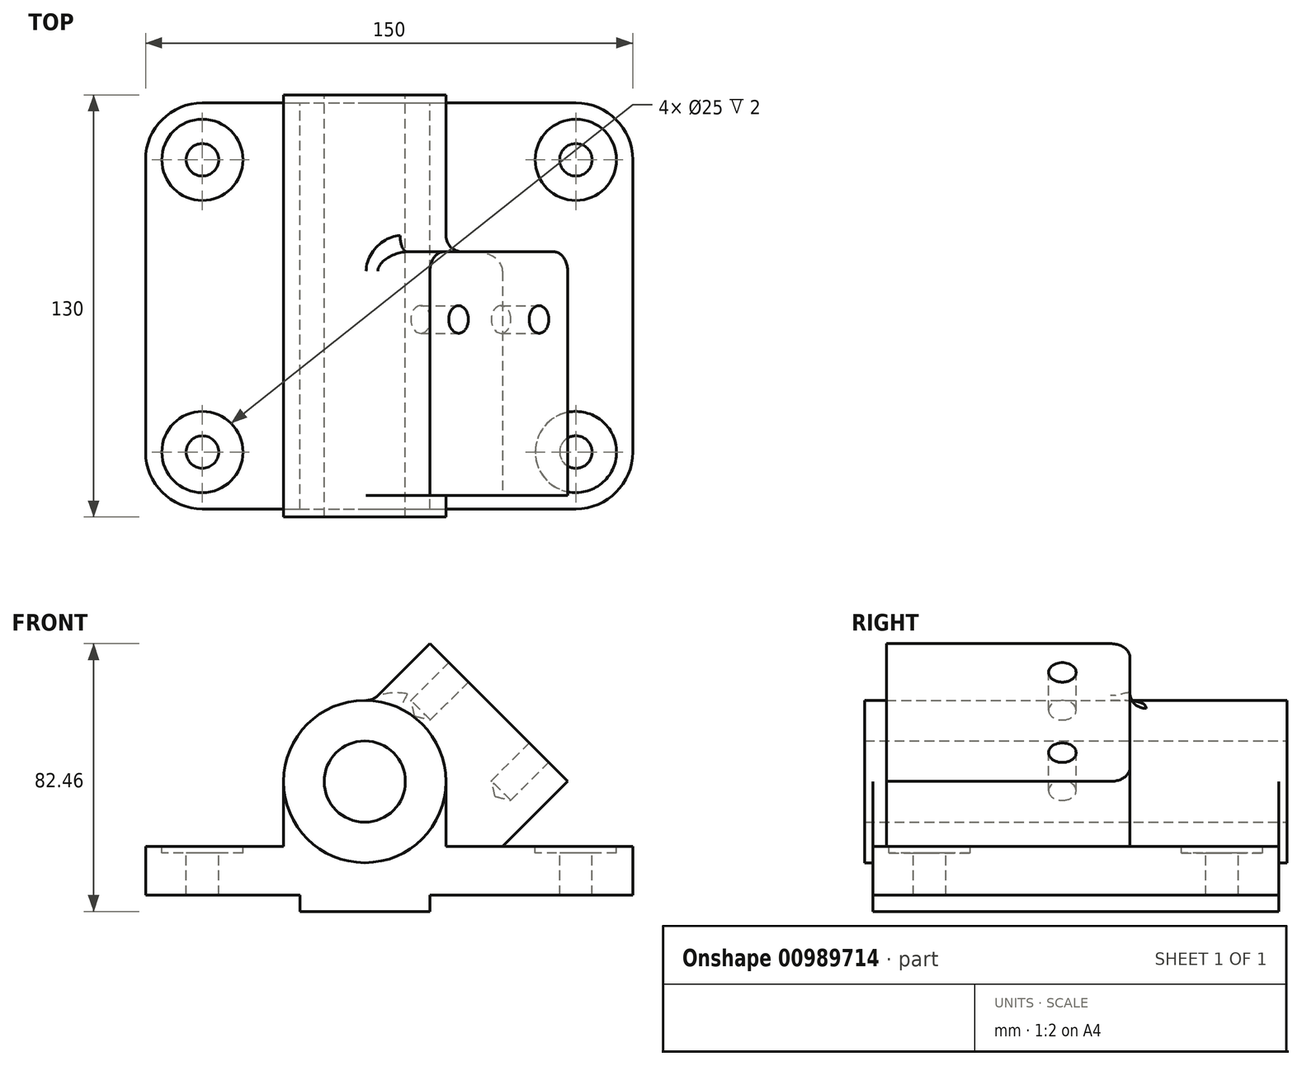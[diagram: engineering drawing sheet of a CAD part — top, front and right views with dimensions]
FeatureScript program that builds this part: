
annotation { "Feature Type Name" : "Feature", "Feature Type Description" : "" }
export const myFeature = defineFeature(function(context is Context, id is Id, definition is map)
    precondition{}
    {
        {
            var Q0;
            Q0=qCreatedBy(makeId("Top.planeOp"),FACE);
            var sketch = newSketch(context, id + "F0", { "sketchPlane" : qUnion([Q0])});
            skLineSegment(sketch, "E0.bottom", {"start": v(-67.5, -62.5) * mm, "end": v(82.5, -62.5) * mm});
            skLineSegment(sketch, "E0.top", {"start": v(-67.5, 62.5) * mm, "end": v(82.5, 62.5) * mm});
            skLineSegment(sketch, "E0.left", {"start": v(-67.5, -62.5) * mm, "end": v(-67.5, 62.5) * mm});
            skLineSegment(sketch, "E0.right", {"start": v(82.5, -62.5) * mm, "end": v(82.5, 62.5) * mm});
            skSolve(sketch);
        }
        {
            var Q0;
            Q0=makeQuery(id+"F0.imprint","IMPRINT",FACE,{"disambiguationData":[TD([[makeQuery(id+"F0.imprint","IMPRINT",EDGE,{"derivedFrom":sQuery(id+"F0.wireOp",EDGE,"E0.bottom")}),1.0]])]});
            extrude(context, id + "F1", {"entities" : qUnion([Q0]), "oppositeDirection" : true, "depth" : 15 * mm, "offsetDistance" : 25 * mm});
        }
        {
            var Q0;
            Q0=qCreatedBy(makeId("Front.planeOp"),FACE);
            var sketch = newSketch(context, id + "F2", { "sketchPlane" : qUnion([Q0])});
            skLineSegment(sketch, "E1.bottom", {"start": v(-20, -15) * mm, "end": v(20, -15) * mm});
            skLineSegment(sketch, "E1.top", {"start": v(-20, -20) * mm, "end": v(20, -20) * mm});
            skLineSegment(sketch, "E1.left", {"start": v(-20, -15) * mm, "end": v(-20, -20) * mm});
            skLineSegment(sketch, "E1.right", {"start": v(20, -15) * mm, "end": v(20, -20) * mm});
            skSolve(sketch);
        }
        {
            var Q0;
            Q0=makeQuery(id+"F2.imprint","IMPRINT",FACE,{"disambiguationData":[TD([[makeQuery(id+"F2.imprint","IMPRINT",EDGE,{"derivedFrom":sQuery(id+"F2.wireOp",EDGE,"E1.bottom")}),-1.0]])]});
            extrude(context, id + "F3", {"entities" : qUnion([Q0]), "operationType" : NewBodyOperationType.ADD, "endBound" : BoundingType.SYMMETRIC, "depth" : (90 + 35) * mm, "offsetDistance" : 25 * mm});
        }
        {
            var Q0;
            Q0=qCreatedBy(makeId("Front.planeOp"),FACE);
            var sketch = newSketch(context, id + "F4", { "sketchPlane" : qUnion([Q0])});
            skLineSegment(sketch, "E2.bottom", {"start": v(-25, 0) * mm, "end": v(25, 0) * mm});
            skLineSegment(sketch, "E2.top", {"start": v(-25, 20) * mm, "end": v(25, 20) * mm});
            skLineSegment(sketch, "E2.left", {"start": v(-25, 0) * mm, "end": v(-25, 20) * mm});
            skLineSegment(sketch, "E2.right", {"start": v(25, 0) * mm, "end": v(25, 20) * mm});
            skCircle(sketch, "E3", {"center": v(0, 20) * mm, "radius": 25 * mm});
            skCircle(sketch, "E4", {"center": v(0, 20) * mm, "radius": 12.5 * mm});
            skSolve(sketch);
        }
        {
            var Q0;
            {var subQ1=sQuery(id+"F4.wireOp",EDGE,"E2.top");var subQ3=sQuery(id+"F4.wireOp",EDGE,"E4");var subQ4=makeQuery(id+"F4.imprint","INTERSECT",VERTEX,{"disambiguationData":[OD(0.0)],"derivedFrom":[subQ1,subQ3]});Q0=makeQuery(id+"F4.imprint","IMPRINT",FACE,{"disambiguationData":[TD([[makeQuery(id+"F4.imprint","IMPRINT",EDGE,{"disambiguationData":[TD([[subQ4,1.0]])],"derivedFrom":subQ3}),-1.0]])]});}
            var Q1;
            {var subQ0=sQuery(id+"F4.wireOp",EDGE,"E3");var subQ3=sQuery(id+"F4.wireOp",EDGE,"E2.bottom");var subQ4=makeQuery(id+"F4.imprint","INTERSECT",VERTEX,{"disambiguationData":[OD(0.0)],"derivedFrom":[subQ3,subQ0]});Q1=makeQuery(id+"F4.imprint","IMPRINT",FACE,{"disambiguationData":[TD([[makeQuery(id+"F4.imprint","IMPRINT",EDGE,{"disambiguationData":[TD([[subQ4,-1.0]])],"derivedFrom":subQ3}),1.0]])]});}
            var Q2;
            {var subQ0=sQuery(id+"F4.wireOp",EDGE,"E3");var subQ1=sQuery(id+"F4.wireOp",EDGE,"E2.bottom");var subQ2=makeQuery(id+"F4.imprint","INTERSECT",VERTEX,{"disambiguationData":[OD(0.0)],"derivedFrom":[subQ1,subQ0]});Q2=makeQuery(id+"F4.imprint","IMPRINT",FACE,{"disambiguationData":[TD([[makeQuery(id+"F4.imprint","IMPRINT",EDGE,{"disambiguationData":[TD([[subQ2,-1.0]])],"derivedFrom":subQ1}),-1.0]])]});}
            extrude(context, id + "F5", {"entities" : qUnion([Q0, Q1, Q2]), "operationType" : NewBodyOperationType.ADD, "endBound" : BoundingType.SYMMETRIC, "depth" : 130 * mm, "offsetDistance" : 25 * mm});
        }
        {
            var Q0;
            {var subQ0=sQuery(id+"F4.wireOp",EDGE,"E2.right");Q0=makeQuery(id+"F4.imprint","IMPRINT",FACE,{"disambiguationData":[TD([[makeQuery(id+"F4.imprint","IMPRINT",EDGE,{"derivedFrom":subQ0}),1.0]])]});}
            var Q1;
            {var subQ0=sQuery(id+"F4.wireOp",EDGE,"E2.left");Q1=makeQuery(id+"F4.imprint","IMPRINT",FACE,{"disambiguationData":[TD([[makeQuery(id+"F4.imprint","IMPRINT",EDGE,{"derivedFrom":subQ0}),-1.0]])]});}
            extrude(context, id + "F6", {"entities" : qUnion([Q0, Q1]), "operationType" : NewBodyOperationType.ADD, "endBound" : BoundingType.SYMMETRIC, "depth" : (90 + 35) * mm, "offsetDistance" : 25 * mm});
        }
        {
            var Q0;
            Q0=makeQuery(id+"F1.opExtrude","CAP_EDGE",EDGE,{"disambiguationData":[OSD([sQuery(id+"F0.wireOp",EDGE,"E0.right")])],"isStart":true});
            var Q1;
            {var subQ4=sQuery(id+"F0.wireOp",EDGE,"E0.top");var subQ5=sQuery(id+"F0.wireOp",EDGE,"E0.right");var subQ6=sQuery(id+"F0.wireOp",EDGE,"E0.bottom");Q1=makeQuery(id+"F5.boolean.opBoolean","SPLIT",FACE,{"disambiguationData":[TD([makeQuery(id+"F1.opExtrude","SWEPT_FACE",FACE,{"disambiguationData":[OSD([subQ5])]})])],"derivedFrom":makeQuery(id+"F1.opExtrude","CAP_FACE",FACE,{"disambiguationData":[OSD([subQ6,subQ4,sQuery(id+"F0.wireOp",EDGE,"E0.left"),subQ5])],"isStart":true})});}
            cPlane(context, id + "F7", {"entities" : qUnion([Q0, Q1]), "cplaneType" : CPlaneType.LINE_ANGLE, "offset" : 25 * mm, "angle" : 45 * degree, "width" : 150 * mm, "height" : 150 * mm});
        }
        {
            var Q0;
            Q0=qCreatedBy(id+"F7.planeOp",FACE);
            var sketch = newSketch(context, id + "F8", { "sketchPlane" : qUnion([Q0])});
            skLineSegment(sketch, "E5.bottom", {"start": v(58.34, 30) * mm, "end": v(-16.66, 30) * mm});
            skLineSegment(sketch, "E5.top", {"start": v(58.34, -30) * mm, "end": v(-16.66, -30) * mm});
            skLineSegment(sketch, "E5.left", {"start": v(58.34, 30) * mm, "end": v(58.34, -30) * mm});
            skLineSegment(sketch, "E5.right", {"start": v(-16.66, 30) * mm, "end": v(-16.66, -30) * mm});
            skSolve(sketch);
        }
        {
            var Q0;
            Q0=makeQuery(id+"F8.imprint","IMPRINT",FACE,{"disambiguationData":[TD([[makeQuery(id+"F8.imprint","IMPRINT",EDGE,{"derivedFrom":sQuery(id+"F8.wireOp",EDGE,"E5.bottom")}),1.0]])]});
            extrude(context, id + "F9", {"entities" : qUnion([Q0]), "operationType" : NewBodyOperationType.ADD, "endBound" : BoundingType.UP_TO_NEXT, "depth" : 25 * mm, "offsetDistance" : 25 * mm});
        }
        {
            var Q0;
            Q0=makeQuery(id+"F9.opExtrude","CAP_FACE",FACE,{"disambiguationData":[OSD([sQuery(id+"F8.wireOp",EDGE,"E5.bottom"),sQuery(id+"F8.wireOp",EDGE,"E5.top"),sQuery(id+"F8.wireOp",EDGE,"E5.left"),sQuery(id+"F8.wireOp",EDGE,"E5.right")])],"isStart":true});
            var sketch = newSketch(context, id + "F10", { "sketchPlane" : qUnion([Q0])});
            skLineSegment(sketch, "E6.bottom", {"start": v(45.84, -17.5) * mm, "end": v(-4.16, -17.5) * mm});
            skLineSegment(sketch, "E6.top", {"start": v(45.84, 17.5) * mm, "end": v(-4.16, 17.5) * mm});
            skLineSegment(sketch, "E6.left", {"start": v(45.84, -17.5) * mm, "end": v(45.84, 17.5) * mm});
            skLineSegment(sketch, "E6.right", {"start": v(-4.16, -17.5) * mm, "end": v(-4.16, 17.5) * mm});
            skLineSegment(sketch, "E7", {"start": v(20.84, -30) * mm, "end": v(20.84, 30) * mm, "construction": true});
            skPoint(sketch, "E8", {"position": v(-4.16, -17.5) * mm});
            skPoint(sketch, "E9", {"position": v(-4.16, 17.5) * mm});
            skPoint(sketch, "E10", {"position": v(45.84, 17.5) * mm});
            skPoint(sketch, "E11", {"position": v(45.84, -17.5) * mm});
            skSolve(sketch);
        }
        {
            var Q0;
            Q0=sQuery(id+"F10.wireOp",VERTEX,"E8");
            var Q1;
            Q1=sQuery(id+"F10.wireOp",VERTEX,"E9");
            var Q2;
            Q2=sQuery(id+"F10.wireOp",VERTEX,"E11");
            var Q3;
            Q3=sQuery(id+"F10.wireOp",VERTEX,"E10");
            var Q4;
            Q4=makeQuery(id+"F1.opExtrude","SWEPT_BODY",BODY,{"disambiguationData":[OSD([sQuery(id+"F0.wireOp",EDGE,"E0.bottom"),sQuery(id+"F0.wireOp",EDGE,"E0.top"),sQuery(id+"F0.wireOp",EDGE,"E0.left"),sQuery(id+"F0.wireOp",EDGE,"E0.right")])]});
            hole(context, id + "F11", {"style" : HoleStyle.SIMPLE, "endStyle" : HoleEndStyle.BLIND, "standardTappedOrClearance" : lookupTablePath({ "standard" : "ISO", "engagement" : "75%", "pitch" : "1.5 mm", "size" : "M10", "type" : "Tapped" }), "standardBlindInLast" : lookupTablePath({ "standard" : "ISO", "fit" : "Normal", "engagement" : "75%", "pitch" : "1.5 mm", "size" : "M10", "type" : "Clearance & tapped" }), "holeDiameter" : 8.5 * mm, "majorDiameter" : 10 * mm, "showTappedDepth" : true, "holeDepth" : 16.5 * mm, "isTappedThrough" : true, "tappedDepth" : 12 * mm, "tapClearance" : 3, "startFromSketch" : true, "locations" : qUnion([Q0, Q1, Q2, Q3]), "scope" : qUnion([Q4])});
        }
        {
            var Q0;
            Q0=makeQuery(id+"F9.opExtrude","CAP_FACE",FACE,{"disambiguationData":[OSD([sQuery(id+"F8.wireOp",EDGE,"E5.bottom"),sQuery(id+"F8.wireOp",EDGE,"E5.top"),sQuery(id+"F8.wireOp",EDGE,"E5.left"),sQuery(id+"F8.wireOp",EDGE,"E5.right")])],"isStart":true});
            var sketch = newSketch(context, id + "F12", { "sketchPlane" : qUnion([Q0])});
            skLineSegment(sketch, "E12", {"start": v(20.84, -30) * mm, "end": v(20.84, 30) * mm, "construction": true});
            skLineSegment(sketch, "E13.bottom", {"start": v(23.84, -30) * mm, "end": v(17.84, -30) * mm});
            skLineSegment(sketch, "E13.top", {"start": v(23.84, 30) * mm, "end": v(17.84, 30) * mm});
            skLineSegment(sketch, "E13.left", {"start": v(23.84, -30) * mm, "end": v(23.84, 30) * mm});
            skLineSegment(sketch, "E13.right", {"start": v(17.84, -30) * mm, "end": v(17.84, 30) * mm});
            skSolve(sketch);
        }
        {
            var Q0;
            Q0=makeQuery(id+"F12.imprint","IMPRINT",FACE,{"disambiguationData":[TD([[makeQuery(id+"F12.imprint","IMPRINT",EDGE,{"derivedFrom":sQuery(id+"F12.wireOp",EDGE,"E13.bottom")}),-1.0]])]});
            extrude(context, id + "F13", {"entities" : qUnion([Q0]), "operationType" : NewBodyOperationType.REMOVE, "oppositeDirection" : true, "depth" : 4 * mm, "offsetDistance" : 25 * mm});
        }
        {
            var Q0;
            Q0=qCreatedBy(makeId("Top.planeOp"),FACE);
            var sketch = newSketch(context, id + "F14", { "sketchPlane" : qUnion([Q0])});
            skLineSegment(sketch, "E14.bottom", {"start": v(-50, -45) * mm, "end": v(65, -45) * mm});
            skLineSegment(sketch, "E14.top", {"start": v(-50, 45) * mm, "end": v(65, 45) * mm});
            skLineSegment(sketch, "E14.left", {"start": v(-50, -45) * mm, "end": v(-50, 45) * mm});
            skLineSegment(sketch, "E14.right", {"start": v(65, -45) * mm, "end": v(65, 45) * mm});
            skPoint(sketch, "E15", {"position": v(-50, -45) * mm});
            skPoint(sketch, "E16", {"position": v(-50, 45) * mm});
            skPoint(sketch, "E17", {"position": v(65, -45) * mm});
            skPoint(sketch, "E18", {"position": v(65, 45) * mm});
            skSolve(sketch);
        }
        {
            var Q0;
            Q0=sQuery(id+"F14.wireOp",VERTEX,"E15");
            var Q1;
            Q1=sQuery(id+"F14.wireOp",VERTEX,"E16");
            var Q2;
            Q2=sQuery(id+"F14.wireOp",VERTEX,"E17");
            var Q3;
            Q3=sQuery(id+"F14.wireOp",VERTEX,"E18");
            var Q4;
            Q4=makeQuery(id+"F1.opExtrude","SWEPT_BODY",BODY,{"disambiguationData":[OSD([sQuery(id+"F0.wireOp",EDGE,"E0.bottom"),sQuery(id+"F0.wireOp",EDGE,"E0.top"),sQuery(id+"F0.wireOp",EDGE,"E0.left"),sQuery(id+"F0.wireOp",EDGE,"E0.right")])]});
            hole(context, id + "F15", {"style" : HoleStyle.C_BORE, "endStyle" : HoleEndStyle.THROUGH, "holeDiameter" : 10 * mm, "cBoreDiameter" : 25 * mm, "cBoreDepth" : 2 * mm, "majorDiameter" : 10 * mm, "isTappedThrough" : true, "tappedDepth" : 12 * mm, "tapClearance" : 3, "startFromSketch" : true, "locations" : qUnion([Q0, Q1, Q2, Q3]), "scope" : qUnion([Q4])});
        }
        {
            var Q0;
            Q0=makeQuery(id+"F1.opExtrude","SWEPT_EDGE",EDGE,{"disambiguationData":[OSD([sQuery(id+"F0.wireOp",EDGE,"E0.bottom"),sQuery(id+"F0.wireOp",EDGE,"E0.left")])]});
            var Q1;
            Q1=makeQuery(id+"F1.opExtrude","SWEPT_EDGE",EDGE,{"disambiguationData":[OSD([sQuery(id+"F0.wireOp",EDGE,"E0.bottom"),sQuery(id+"F0.wireOp",EDGE,"E0.right")])]});
            var Q2;
            Q2=makeQuery(id+"F1.opExtrude","SWEPT_EDGE",EDGE,{"disambiguationData":[OSD([sQuery(id+"F0.wireOp",EDGE,"E0.top"),sQuery(id+"F0.wireOp",EDGE,"E0.right")])]});
            var Q3;
            Q3=makeQuery(id+"F1.opExtrude","SWEPT_EDGE",EDGE,{"disambiguationData":[OSD([sQuery(id+"F0.wireOp",EDGE,"E0.top"),sQuery(id+"F0.wireOp",EDGE,"E0.left")])]});
            fillet(context, id + "F16", {"entities" : qUnion([Q0, Q1, Q2, Q3]), "radius" : 17.5 * mm, "tangentPropagation" : true, "allowEdgeOverflow" : false});
        }
        {
            var Q0;
            Q0=makeQuery(id+"F9.opExtrude","SWEPT_EDGE",EDGE,{"disambiguationData":[OSD([sQuery(id+"F8.wireOp",EDGE,"E5.top"),sQuery(id+"F8.wireOp",EDGE,"E5.right")])]});
            var Q1;
            Q1=makeQuery(id+"F9.opExtrude","SWEPT_EDGE",EDGE,{"disambiguationData":[OSD([sQuery(id+"F8.wireOp",EDGE,"E5.bottom"),sQuery(id+"F8.wireOp",EDGE,"E5.right")])]});
            fillet(context, id + "F17", {"entities" : qUnion([Q0, Q1]), "radius" : 6 * mm, "tangentPropagation" : true, "allowEdgeOverflow" : false});
        }
        {
            var Q0;
            Q0=makeQuery(id+"F9.opExtrude","CAP_EDGE",EDGE,{"disambiguationData":[OSD([sQuery(id+"F8.wireOp",EDGE,"E5.right")])],"isStart":false});
            var Q1;
            {var subQ1=sQuery(id+"F4.wireOp",EDGE,"E2.bottom");var subQ2=sQuery(id+"F0.wireOp",EDGE,"E0.top");var subQ3=sQuery(id+"F4.wireOp",EDGE,"E2.right");Q1=makeQuery(id+"F9.boolean.opBoolean","SPLIT",EDGE,{"disambiguationData":[TD([makeQuery(id+"F1.opExtrude","SWEPT_FACE",FACE,{"disambiguationData":[OSD([subQ2])]})])],"derivedFrom":makeQuery(id+"F6.opExtrude","SWEPT_EDGE",EDGE,{"disambiguationData":[OSD([subQ1,subQ3])]})});}
            var Q2;
            {var subQ1=sQuery(id+"F4.wireOp",EDGE,"E2.bottom");var subQ2=sQuery(id+"F0.wireOp",EDGE,"E0.bottom");var subQ3=sQuery(id+"F4.wireOp",EDGE,"E2.right");Q2=makeQuery(id+"F9.boolean.opBoolean","SPLIT",EDGE,{"disambiguationData":[TD([makeQuery(id+"F1.opExtrude","SWEPT_FACE",FACE,{"disambiguationData":[OSD([subQ2])]})])],"derivedFrom":makeQuery(id+"F6.opExtrude","SWEPT_EDGE",EDGE,{"disambiguationData":[OSD([subQ1,subQ3])]})});}
            var Q3;
            Q3=makeQuery(id+"F6.opExtrude","SWEPT_EDGE",EDGE,{"disambiguationData":[OSD([sQuery(id+"F4.wireOp",EDGE,"E2.bottom"),sQuery(id+"F4.wireOp",EDGE,"E2.left")])]});
            fillet(context, id + "F18", {"entities" : qUnion([Q0, Q1, Q2, Q3]), "radius" : 5 * mm, "tangentPropagation" : true, "allowEdgeOverflow" : false});
        }
    });
